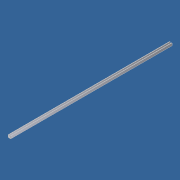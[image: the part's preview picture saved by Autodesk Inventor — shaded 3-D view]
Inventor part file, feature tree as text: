
AUTODESK INVENTOR PART (.ipt)
format: ipt  version: 2012 (Build 160160000, 160)  size: 74,240 bytes
history: native  units: in
note: dims shown in document units (in); Inventor stores cm internally (conversion verified against a paired STEP export)
features: extrude x1, sketch x1
ambient origin geometry x8: Origin, YZ Plane, XZ Plane, XY Plane, X Axis, Y Axis, Z Axis, Center Point
bodies: Solid1 (feature_tree)
feature tree (2):
  extrude  "Extrusion1"  Depth=0.125in
  sketch  "Sketch1"  dims[d0=0.5in d2=0.125in d3=0.125in d4=0.75in d5=0.625in d6=0.625in d7=48.75in d8=0.0in]
